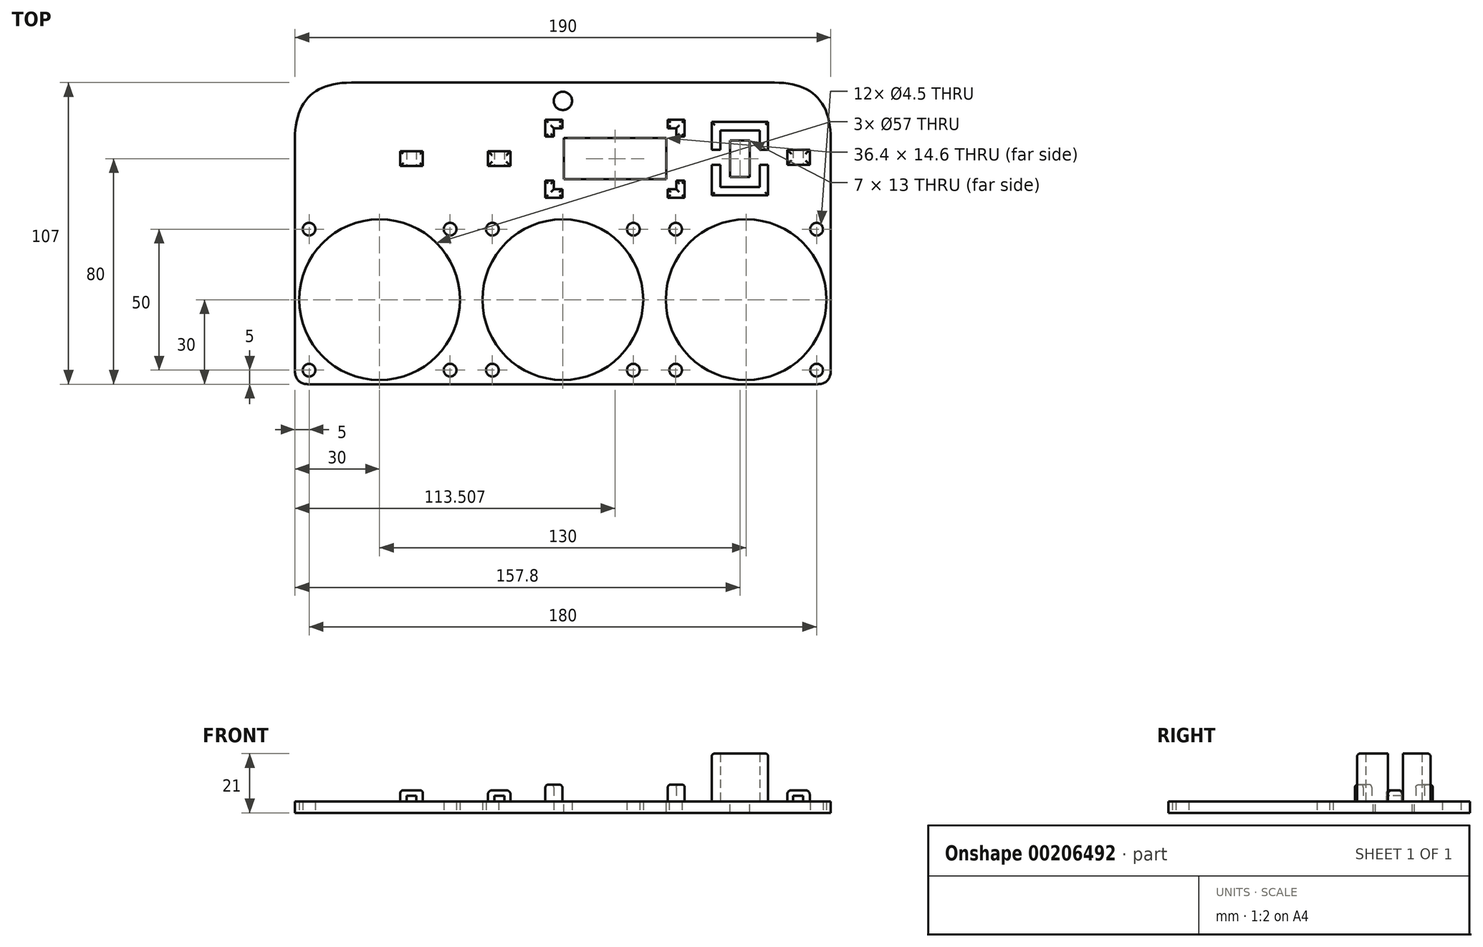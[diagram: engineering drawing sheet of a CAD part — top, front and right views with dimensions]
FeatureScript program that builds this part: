
annotation { "Feature Type Name" : "Feature", "Feature Type Description" : "" }
export const myFeature = defineFeature(function(context is Context, id is Id, definition is map)
    precondition{}
    {
        {
            var Q0;
            Q0=qCreatedBy(makeId("Top.planeOp"),FACE);
            var sketch = newSketch(context, id + "F0", { "sketchPlane" : qUnion([Q0])});
            skLineSegment(sketch, "E0", {"start": v(0, 124.98) * mm, "end": v(0, -119.8) * mm, "construction": true});
            skLineSegment(sketch, "E1.bottom", {"start": v(0, 0) * mm, "end": v(60, 0) * mm});
            skLineSegment(sketch, "E1.left", {"start": v(0, 0) * mm, "end": v(0, 60) * mm});
            skLineSegment(sketch, "E2.bottom", {"start": v(5, 5) * mm, "end": v(55, 5) * mm, "construction": true});
            skLineSegment(sketch, "E2.top", {"start": v(5, 55) * mm, "end": v(55, 55) * mm, "construction": true});
            skLineSegment(sketch, "E2.left", {"start": v(5, 5) * mm, "end": v(5, 55) * mm, "construction": true});
            skLineSegment(sketch, "E2.right", {"start": v(55, 5) * mm, "end": v(55, 55) * mm, "construction": true});
            skPoint(sketch, "E3.centerSnap0", {"position": v(55, 30) * mm});
            skPoint(sketch, "E3.centerSnap1", {"position": v(30, 55) * mm});
            skLineSegment(sketch, "E4.bottom", {"start": v(65, 0) * mm, "end": v(125, 0) * mm});
            skLineSegment(sketch, "E5.bottom", {"start": v(70, 5) * mm, "end": v(120, 5) * mm, "construction": true});
            skLineSegment(sketch, "E5.top", {"start": v(70, 55) * mm, "end": v(120, 55) * mm, "construction": true});
            skLineSegment(sketch, "E5.left", {"start": v(70, 5) * mm, "end": v(70, 55) * mm, "construction": true});
            skLineSegment(sketch, "E5.right", {"start": v(120, 5) * mm, "end": v(120, 55) * mm, "construction": true});
            skCircle(sketch, "E6", {"center": v(95, 30) * mm, "radius": 28.5 * mm});
            skPoint(sketch, "E6.centerSnap0", {"position": v(120, 30) * mm});
            skPoint(sketch, "E6.centerSnap1", {"position": v(95, 55) * mm});
            skLineSegment(sketch, "E7.bottom", {"start": v(130, 0) * mm, "end": v(190, 0) * mm});
            skLineSegment(sketch, "E7.right", {"start": v(190, 0) * mm, "end": v(190, 60) * mm});
            skLineSegment(sketch, "E8.bottom", {"start": v(135, 5) * mm, "end": v(185, 5) * mm, "construction": true});
            skLineSegment(sketch, "E8.top", {"start": v(135, 55) * mm, "end": v(185, 55) * mm, "construction": true});
            skLineSegment(sketch, "E8.left", {"start": v(135, 5) * mm, "end": v(135, 55) * mm, "construction": true});
            skLineSegment(sketch, "E8.right", {"start": v(185, 5) * mm, "end": v(185, 55) * mm, "construction": true});
            skCircle(sketch, "E9", {"center": v(160, 30) * mm, "radius": 28.5 * mm});
            skPoint(sketch, "E9.centerSnap0", {"position": v(185, 30) * mm});
            skPoint(sketch, "E9.centerSnap1", {"position": v(160, 55) * mm});
            skLineSegment(sketch, "E10", {"start": v(60, 0) * mm, "end": v(65, 0) * mm});
            skLineSegment(sketch, "E11", {"start": v(125, 0) * mm, "end": v(130, 0) * mm});
            skLineSegment(sketch, "E12.top", {"start": v(0, 107) * mm, "end": v(190, 107) * mm});
            skLineSegment(sketch, "E12.left", {"start": v(0, 60) * mm, "end": v(0, 107) * mm});
            skLineSegment(sketch, "E12.right", {"start": v(190, 60) * mm, "end": v(190, 107) * mm});
            skLineSegment(sketch, "E13", {"start": v(95, 107) * mm, "end": v(95, -15.16) * mm, "construction": true});
            skLineSegment(sketch, "E14", {"start": v(95, 100.5) * mm, "end": v(107.18, 100.5) * mm, "construction": true});
            skCircle(sketch, "E15", {"center": v(30, 30) * mm, "radius": 28.5 * mm});
            skSolve(sketch);
        }
        {
            var Q0;
            Q0=qSketchRegion(id+"F0",true);
            extrude(context, id + "F1", {"entities" : qUnion([Q0]), "depth" : 4 * mm});
        }
        {
            var Q0;
            Q0=sQuery(id+"F0.wireOp",VERTEX,"E14.start");
            var Q1;
            Q1=makeQuery(id+"F1.opExtrude","SWEPT_BODY",BODY,{"disambiguationData":[OSD([sQuery(id+"F0.wireOp",EDGE,"E1.bottom"),sQuery(id+"F0.wireOp",EDGE,"E1.left"),sQuery(id+"F0.wireOp",EDGE,"E3"),sQuery(id+"F0.wireOp",EDGE,"E4.bottom"),sQuery(id+"F0.wireOp",EDGE,"E6"),sQuery(id+"F0.wireOp",EDGE,"E7.bottom"),sQuery(id+"F0.wireOp",EDGE,"E7.right"),sQuery(id+"F0.wireOp",EDGE,"E9"),sQuery(id+"F0.wireOp",EDGE,"E10"),sQuery(id+"F0.wireOp",EDGE,"E11"),sQuery(id+"F0.wireOp",EDGE,"E12.top"),sQuery(id+"F0.wireOp",EDGE,"E12.left"),sQuery(id+"F0.wireOp",EDGE,"E12.right")])]});
            hole(context, id + "F2", {"style" : HoleStyle.SIMPLE, "endStyle" : HoleEndStyle.THROUGH, "oppositeDirection" : true, "holeDiameter" : 6.5 * mm, "locations" : qUnion([Q0]), "scope" : qUnion([Q1]), "isTappedThrough" : true});
        }
        {
            var Q0;
            Q0=sQuery(id+"F0.wireOp",VERTEX,"E2.top.start");
            var Q1;
            Q1=sQuery(id+"F0.wireOp",VERTEX,"E2.top.end");
            var Q2;
            Q2=sQuery(id+"F0.wireOp",VERTEX,"E2.bottom.start");
            var Q3;
            Q3=sQuery(id+"F0.wireOp",VERTEX,"E2.bottom.end");
            var Q4;
            Q4=sQuery(id+"F0.wireOp",VERTEX,"E5.left.end");
            var Q5;
            Q5=sQuery(id+"F0.wireOp",VERTEX,"E5.bottom.start");
            var Q6;
            Q6=sQuery(id+"F0.wireOp",VERTEX,"E5.bottom.end");
            var Q7;
            Q7=sQuery(id+"F0.wireOp",VERTEX,"E5.top.end");
            var Q8;
            Q8=sQuery(id+"F0.wireOp",VERTEX,"E8.left.end");
            var Q9;
            Q9=sQuery(id+"F0.wireOp",VERTEX,"E8.bottom.start");
            var Q10;
            Q10=sQuery(id+"F0.wireOp",VERTEX,"E8.bottom.end");
            var Q11;
            Q11=sQuery(id+"F0.wireOp",VERTEX,"E8.top.end");
            var Q12;
            Q12=makeQuery(id+"F1.opExtrude","SWEPT_BODY",BODY,{"disambiguationData":[OSD([sQuery(id+"F0.wireOp",EDGE,"E1.bottom"),sQuery(id+"F0.wireOp",EDGE,"E1.left"),sQuery(id+"F0.wireOp",EDGE,"E3"),sQuery(id+"F0.wireOp",EDGE,"E4.bottom"),sQuery(id+"F0.wireOp",EDGE,"E6"),sQuery(id+"F0.wireOp",EDGE,"E7.bottom"),sQuery(id+"F0.wireOp",EDGE,"E7.right"),sQuery(id+"F0.wireOp",EDGE,"E9"),sQuery(id+"F0.wireOp",EDGE,"E10"),sQuery(id+"F0.wireOp",EDGE,"E11"),sQuery(id+"F0.wireOp",EDGE,"E12.top"),sQuery(id+"F0.wireOp",EDGE,"E12.left"),sQuery(id+"F0.wireOp",EDGE,"E12.right")])]});
            hole(context, id + "F3", {"style" : HoleStyle.SIMPLE, "endStyle" : HoleEndStyle.THROUGH, "oppositeDirection" : true, "holeDiameter" : 4.5 * mm, "locations" : qUnion([Q0, Q1, Q2, Q3, Q4, Q5, Q6, Q7, Q8, Q9, Q10, Q11]), "scope" : qUnion([Q12]), "isTappedThrough" : true});
        }
        {
            var Q0;
            Q0=makeQuery(id+"F1.opExtrude","CAP_FACE",FACE,{"disambiguationData":[OSD([sQuery(id+"F0.wireOp",EDGE,"E1.bottom"),sQuery(id+"F0.wireOp",EDGE,"E1.left"),sQuery(id+"F0.wireOp",EDGE,"E3"),sQuery(id+"F0.wireOp",EDGE,"E4.bottom"),sQuery(id+"F0.wireOp",EDGE,"E6"),sQuery(id+"F0.wireOp",EDGE,"E7.bottom"),sQuery(id+"F0.wireOp",EDGE,"E7.right"),sQuery(id+"F0.wireOp",EDGE,"E9"),sQuery(id+"F0.wireOp",EDGE,"E10"),sQuery(id+"F0.wireOp",EDGE,"E11"),sQuery(id+"F0.wireOp",EDGE,"E12.top"),sQuery(id+"F0.wireOp",EDGE,"E12.left"),sQuery(id+"F0.wireOp",EDGE,"E12.right")])],"isStart":false});
            var sketch = newSketch(context, id + "F4", { "sketchPlane" : qUnion([Q0])});
            skLineSegment(sketch, "E16", {"start": v(160, 30) * mm, "end": v(160, 156.78) * mm, "construction": true});
            skLineSegment(sketch, "E17.bottom", {"start": v(150.8, 90) * mm, "end": v(164.8, 90) * mm});
            skLineSegment(sketch, "E17.top", {"start": v(150.8, 70) * mm, "end": v(164.8, 70) * mm});
            skLineSegment(sketch, "E17.left", {"start": v(150.8, 90) * mm, "end": v(150.8, 83.18) * mm});
            skLineSegment(sketch, "E17.right", {"start": v(164.8, 90) * mm, "end": v(164.8, 83.18) * mm});
            skLineSegment(sketch, "E18.0", {"start": v(147.8, 93) * mm, "end": v(147.8, 83.18) * mm});
            skLineSegment(sketch, "E18.1", {"start": v(147.8, 93) * mm, "end": v(167.8, 93) * mm});
            skLineSegment(sketch, "E18.2", {"start": v(167.8, 93) * mm, "end": v(167.8, 83.18) * mm});
            skLineSegment(sketch, "E18.3", {"start": v(147.8, 67) * mm, "end": v(167.8, 67) * mm});
            skLineSegment(sketch, "E19.0", {"start": v(185, 102) * mm, "end": v(5, 102) * mm});
            skLineSegment(sketch, "E19.1", {"start": v(185, 5) * mm, "end": v(185, 102) * mm});
            skLineSegment(sketch, "E19.2", {"start": v(5, 5) * mm, "end": v(185, 5) * mm});
            skLineSegment(sketch, "E19.3", {"start": v(5, 102) * mm, "end": v(5, 5) * mm});
            skLineSegment(sketch, "E20", {"start": v(164.8, 83.18) * mm, "end": v(167.8, 83.18) * mm});
            skLineSegment(sketch, "E21", {"start": v(164.8, 77.87) * mm, "end": v(167.8, 77.87) * mm});
            skLineSegment(sketch, "E22", {"start": v(150.8, 77.87) * mm, "end": v(147.8, 77.87) * mm});
            skLineSegment(sketch, "E23", {"start": v(150.8, 83.18) * mm, "end": v(147.8, 83.18) * mm});
            skLineSegment(sketch, "E24.trimOffspring", {"start": v(147.8, 77.87) * mm, "end": v(147.8, 67) * mm});
            skLineSegment(sketch, "E25.trimOffspring", {"start": v(150.8, 77.87) * mm, "end": v(150.8, 70) * mm});
            skLineSegment(sketch, "E26.trimOffspring", {"start": v(164.8, 77.87) * mm, "end": v(164.8, 70) * mm});
            skLineSegment(sketch, "E27.trimOffspring", {"start": v(167.8, 77.87) * mm, "end": v(167.8, 67) * mm});
            skLineSegment(sketch, "E28", {"start": v(91.8, 87.8) * mm, "end": v(91.8, 90.8) * mm});
            skLineSegment(sketch, "E29", {"start": v(91.8, 90.8) * mm, "end": v(94.8, 90.8) * mm});
            skLineSegment(sketch, "E30", {"start": v(94.8, 90.8) * mm, "end": v(94.8, 93.8) * mm});
            skLineSegment(sketch, "E31", {"start": v(94.8, 93.8) * mm, "end": v(88.8, 93.8) * mm});
            skLineSegment(sketch, "E32", {"start": v(88.8, 93.8) * mm, "end": v(88.8, 87.8) * mm});
            skLineSegment(sketch, "E33", {"start": v(88.8, 87.8) * mm, "end": v(91.8, 87.8) * mm});
            skLineSegment(sketch, "E34", {"start": v(82.5, 80) * mm, "end": v(142.35, 80) * mm, "construction": true});
            skLineSegment(sketch, "E35", {"start": v(113.5, 100.09) * mm, "end": v(113.5, 63.62) * mm, "construction": true});
            skLineSegment(sketch, "E36.MirrorCS", {"start": v(94.8, 66.2) * mm, "end": v(88.8, 66.2) * mm});
            skLineSegment(sketch, "E37.MirrorCS", {"start": v(94.8, 69.2) * mm, "end": v(94.8, 66.2) * mm});
            skLineSegment(sketch, "E38.MirrorCS", {"start": v(91.8, 69.2) * mm, "end": v(94.8, 69.2) * mm});
            skLineSegment(sketch, "E39.MirrorCS", {"start": v(88.8, 66.2) * mm, "end": v(88.8, 72.2) * mm});
            skLineSegment(sketch, "E40.MirrorCS", {"start": v(88.8, 72.2) * mm, "end": v(91.8, 72.2) * mm});
            skLineSegment(sketch, "E41.MirrorCS", {"start": v(91.8, 72.2) * mm, "end": v(91.8, 69.2) * mm});
            skLineSegment(sketch, "E42.MirrorCS", {"start": v(138.2, 72.2) * mm, "end": v(135.2, 72.2) * mm});
            skLineSegment(sketch, "E43.MirrorCS", {"start": v(132.2, 66.2) * mm, "end": v(138.2, 66.2) * mm});
            skLineSegment(sketch, "E44.MirrorCS", {"start": v(138.2, 66.2) * mm, "end": v(138.2, 72.2) * mm});
            skLineSegment(sketch, "E45.MirrorCS", {"start": v(135.2, 69.2) * mm, "end": v(132.2, 69.2) * mm});
            skLineSegment(sketch, "E46.MirrorCS", {"start": v(135.2, 72.2) * mm, "end": v(135.2, 69.2) * mm});
            skLineSegment(sketch, "E47.MirrorCS", {"start": v(132.2, 69.2) * mm, "end": v(132.2, 66.2) * mm});
            skLineSegment(sketch, "E48.MirrorCS", {"start": v(132.2, 90.8) * mm, "end": v(132.2, 93.8) * mm});
            skLineSegment(sketch, "E49.MirrorCS", {"start": v(138.2, 87.8) * mm, "end": v(135.2, 87.8) * mm});
            skLineSegment(sketch, "E50.MirrorCS", {"start": v(135.2, 87.8) * mm, "end": v(135.2, 90.8) * mm});
            skLineSegment(sketch, "E51.MirrorCS", {"start": v(138.2, 93.8) * mm, "end": v(138.2, 87.8) * mm});
            skLineSegment(sketch, "E52.MirrorCS", {"start": v(135.2, 90.8) * mm, "end": v(132.2, 90.8) * mm});
            skLineSegment(sketch, "E53.MirrorCS", {"start": v(132.2, 93.8) * mm, "end": v(138.2, 93.8) * mm});
            skPoint(sketch, "E54.firstSnap0", {"position": v(135.2, 93.8) * mm});
            skLineSegment(sketch, "E55.bottom", {"start": v(91.8, 90.8) * mm, "end": v(135.2, 90.8) * mm, "construction": true});
            skLineSegment(sketch, "E55.top", {"start": v(91.8, 69.2) * mm, "end": v(135.2, 69.2) * mm, "construction": true});
            skLineSegment(sketch, "E55.left", {"start": v(91.8, 90.8) * mm, "end": v(91.8, 69.2) * mm, "construction": true});
            skLineSegment(sketch, "E55.right", {"start": v(135.2, 90.8) * mm, "end": v(135.2, 69.2) * mm, "construction": true});
            skLineSegment(sketch, "E56.0", {"start": v(95.3, 87.3) * mm, "end": v(131.7, 87.3) * mm});
            skLineSegment(sketch, "E56.1", {"start": v(95.3, 87.3) * mm, "end": v(95.3, 72.7) * mm});
            skLineSegment(sketch, "E56.2", {"start": v(95.3, 72.7) * mm, "end": v(131.7, 72.7) * mm});
            skLineSegment(sketch, "E56.3", {"start": v(131.7, 87.3) * mm, "end": v(131.7, 72.7) * mm});
            skLineSegment(sketch, "E57.left", {"start": v(150.8, 90) * mm, "end": v(150.8, 70) * mm});
            skLineSegment(sketch, "E57.right", {"start": v(164.8, 90) * mm, "end": v(164.8, 70) * mm});
            skLineSegment(sketch, "E58.0", {"start": v(154.3, 86.5) * mm, "end": v(154.3, 73.5) * mm});
            skLineSegment(sketch, "E58.1", {"start": v(154.3, 86.5) * mm, "end": v(161.3, 86.5) * mm});
            skLineSegment(sketch, "E58.2", {"start": v(161.3, 86.5) * mm, "end": v(161.3, 73.5) * mm});
            skLineSegment(sketch, "E58.3", {"start": v(154.3, 73.5) * mm, "end": v(161.3, 73.5) * mm});
            skPoint(sketch, "E59", {"position": v(150.8, 80) * mm});
            skLineSegment(sketch, "E60.bottom", {"start": v(174.55, 83.18) * mm, "end": v(182.55, 83.18) * mm});
            skLineSegment(sketch, "E60.top", {"start": v(174.55, 77.87) * mm, "end": v(182.55, 77.87) * mm});
            skLineSegment(sketch, "E60.left", {"start": v(174.55, 83.18) * mm, "end": v(174.55, 77.87) * mm});
            skLineSegment(sketch, "E60.right", {"start": v(182.55, 83.18) * mm, "end": v(182.55, 77.87) * mm});
            skLineSegment(sketch, "E61.bottom", {"start": v(68.44, 82.7) * mm, "end": v(76.44, 82.7) * mm});
            skLineSegment(sketch, "E61.top", {"start": v(68.44, 77.4) * mm, "end": v(76.44, 77.4) * mm});
            skLineSegment(sketch, "E61.left", {"start": v(68.44, 82.7) * mm, "end": v(68.44, 77.4) * mm});
            skLineSegment(sketch, "E61.right", {"start": v(76.44, 82.7) * mm, "end": v(76.44, 77.4) * mm});
            skLineSegment(sketch, "E62.bottom", {"start": v(45.36, 77.4) * mm, "end": v(37.36, 77.4) * mm});
            skLineSegment(sketch, "E62.top", {"start": v(45.36, 82.7) * mm, "end": v(37.36, 82.7) * mm});
            skLineSegment(sketch, "E62.left", {"start": v(45.36, 77.4) * mm, "end": v(45.36, 82.7) * mm});
            skLineSegment(sketch, "E62.right", {"start": v(37.36, 77.4) * mm, "end": v(37.36, 82.7) * mm});
            skSolve(sketch);
        }
        {
            var Q0;
            Q0=makeQuery(id+"F4.imprint","IMPRINT",FACE,{"disambiguationData":[TD([[makeQuery(id+"F4.imprint","IMPRINT",EDGE,{"derivedFrom":sQuery(id+"F4.wireOp",EDGE,"E18.0")}),1.0]])]});
            var Q1;
            Q1=makeQuery(id+"F4.imprint","IMPRINT",FACE,{"disambiguationData":[TD([[makeQuery(id+"F4.imprint","IMPRINT",EDGE,{"derivedFrom":sQuery(id+"F4.wireOp",EDGE,"E18.3")}),1.0]])]});
            extrude(context, id + "F5", {"entities" : qUnion([Q0, Q1]), "operationType" : NewBodyOperationType.ADD, "depth" : 17 * mm});
        }
        {
            var Q0;
            Q0=makeQuery(id+"F4.imprint","IMPRINT",FACE,{"disambiguationData":[TD([[makeQuery(id+"F4.imprint","IMPRINT",EDGE,{"derivedFrom":sQuery(id+"F4.wireOp",EDGE,"E48.MirrorCS")}),-1.0]])]});
            var Q1;
            Q1=makeQuery(id+"F4.imprint","IMPRINT",FACE,{"disambiguationData":[TD([[makeQuery(id+"F4.imprint","IMPRINT",EDGE,{"derivedFrom":sQuery(id+"F4.wireOp",EDGE,"E42.MirrorCS")}),1.0]])]});
            var Q2;
            Q2=makeQuery(id+"F4.imprint","IMPRINT",FACE,{"disambiguationData":[TD([[makeQuery(id+"F4.imprint","IMPRINT",EDGE,{"derivedFrom":sQuery(id+"F4.wireOp",EDGE,"E36.MirrorCS")}),-1.0]])]});
            var Q3;
            Q3=makeQuery(id+"F4.imprint","IMPRINT",FACE,{"disambiguationData":[TD([[makeQuery(id+"F4.imprint","IMPRINT",EDGE,{"derivedFrom":sQuery(id+"F4.wireOp",EDGE,"E28")}),1.0]])]});
            extrude(context, id + "F6", {"entities" : qUnion([Q0, Q1, Q2, Q3]), "operationType" : NewBodyOperationType.ADD, "depth" : 6 * mm});
        }
        {
            var Q0;
            Q0=makeQuery(id+"F4.imprint","IMPRINT",FACE,{"disambiguationData":[TD([[makeQuery(id+"F4.imprint","IMPRINT",EDGE,{"derivedFrom":sQuery(id+"F4.wireOp",EDGE,"E56.0")}),-1.0]])]});
            extrude(context, id + "F7", {"entities" : qUnion([Q0]), "operationType" : NewBodyOperationType.REMOVE, "oppositeDirection" : true, "depth" : 25 * mm});
        }
        {
            var Q0;
            Q0=makeQuery(id+"F4.imprint","IMPRINT",FACE,{"disambiguationData":[TD([[makeQuery(id+"F4.imprint","IMPRINT",EDGE,{"derivedFrom":sQuery(id+"F4.wireOp",EDGE,"E58.0")}),1.0]])]});
            extrude(context, id + "F8", {"entities" : qUnion([Q0]), "operationType" : NewBodyOperationType.REMOVE, "oppositeDirection" : true, "depth" : 25 * mm});
        }
        {
            var Q0;
            Q0=makeQuery(id+"F1.opExtrude","SWEPT_EDGE",EDGE,{"disambiguationData":[OSD([sQuery(id+"F0.wireOp",EDGE,"E12.top"),sQuery(id+"F0.wireOp",EDGE,"E12.left")])]});
            var Q1;
            Q1=makeQuery(id+"F1.opExtrude","SWEPT_EDGE",EDGE,{"disambiguationData":[OSD([sQuery(id+"F0.wireOp",EDGE,"E12.top"),sQuery(id+"F0.wireOp",EDGE,"E12.right")])]});
            fillet(context, id + "F9", {"entities" : qUnion([Q0, Q1]), "radius" : 20 * mm, "tangentPropagation" : true, "rho" : 0.5, "crossSection" : FilletCrossSection.CONIC, "allowEdgeOverflow" : false});
        }
        {
            var Q0;
            Q0=makeQuery(id+"F1.opExtrude","SWEPT_EDGE",EDGE,{"disambiguationData":[OSD([sQuery(id+"F0.wireOp",EDGE,"E1.bottom"),sQuery(id+"F0.wireOp",EDGE,"E1.left")])]});
            var Q1;
            Q1=makeQuery(id+"F1.opExtrude","SWEPT_EDGE",EDGE,{"disambiguationData":[OSD([sQuery(id+"F0.wireOp",EDGE,"E7.bottom"),sQuery(id+"F0.wireOp",EDGE,"E7.right")])]});
            fillet(context, id + "F10", {"entities" : qUnion([Q0, Q1]), "radius" : 5 * mm, "tangentPropagation" : true, "rho" : 0.5, "crossSection" : FilletCrossSection.CONIC, "allowEdgeOverflow" : false});
        }
        {
            var Q0;
            Q0=makeQuery(id+"F4.imprint","IMPRINT",FACE,{"disambiguationData":[TD([[makeQuery(id+"F4.imprint","IMPRINT",EDGE,{"derivedFrom":sQuery(id+"F4.wireOp",EDGE,"E60.bottom")}),-1.0]])]});
            var Q1;
            Q1=makeQuery(id+"F4.imprint","IMPRINT",FACE,{"disambiguationData":[TD([[makeQuery(id+"F4.imprint","IMPRINT",EDGE,{"derivedFrom":sQuery(id+"F4.wireOp",EDGE,"E61.bottom")}),-1.0]])]});
            var Q2;
            Q2=makeQuery(id+"F4.imprint","IMPRINT",FACE,{"disambiguationData":[TD([[makeQuery(id+"F4.imprint","IMPRINT",EDGE,{"derivedFrom":sQuery(id+"F4.wireOp",EDGE,"E62.bottom")}),-1.0]])]});
            extrude(context, id + "F11", {"entities" : qUnion([Q0, Q1, Q2]), "operationType" : NewBodyOperationType.ADD, "depth" : 4 * mm});
        }
        {
            var Q0;
            Q0=makeQuery(id+"F11.opExtrude","SWEPT_FACE",FACE,{"disambiguationData":[OSD([sQuery(id+"F4.wireOp",EDGE,"E60.top")])]});
            var sketch = newSketch(context, id + "F12", { "sketchPlane" : qUnion([Q0])});
            skPoint(sketch, "E63.oppositeSnap0", {"position": v(174.55, 6) * mm});
            skLineSegment(sketch, "E63.bottom", {"start": v(176.7, 4) * mm, "end": v(180.23, 4) * mm});
            skLineSegment(sketch, "E63.top", {"start": v(176.7, 6) * mm, "end": v(180.23, 6) * mm});
            skLineSegment(sketch, "E63.left", {"start": v(176.7, 4) * mm, "end": v(176.7, 6) * mm});
            skLineSegment(sketch, "E63.right", {"start": v(180.23, 4) * mm, "end": v(180.23, 6) * mm});
            skSolve(sketch);
        }
        {
            var Q0;
            Q0=qSketchRegion(id+"F12",true);
            extrude(context, id + "F13", {"entities" : qUnion([Q0]), "operationType" : NewBodyOperationType.REMOVE, "oppositeDirection" : true, "depth" : 25 * mm});
        }
        {
            var Q0;
            Q0=makeQuery(id+"F11.opExtrude","CAP_EDGE",EDGE,{"disambiguationData":[OSD([sQuery(id+"F4.wireOp",EDGE,"E60.left")])],"isStart":false});
            var Q1;
            Q1=makeQuery(id+"F11.opExtrude","CAP_EDGE",EDGE,{"disambiguationData":[OSD([sQuery(id+"F4.wireOp",EDGE,"E60.right")])],"isStart":false});
            var Q2;
            Q2=makeQuery(id+"F11.opExtrude","CAP_EDGE",EDGE,{"disambiguationData":[OSD([sQuery(id+"F4.wireOp",EDGE,"E60.bottom")])],"isStart":false});
            var Q3;
            Q3=makeQuery(id+"F11.opExtrude","CAP_EDGE",EDGE,{"disambiguationData":[OSD([sQuery(id+"F4.wireOp",EDGE,"E60.top")])],"isStart":false});
            fillet(context, id + "F14", {"entities" : qUnion([Q0, Q1, Q2, Q3]), "radius" : 1.5 * mm, "tangentPropagation" : true, "allowEdgeOverflow" : false});
        }
        {
            var Q0;
            Q0=makeQuery(id+"F5.opExtrude","CAP_EDGE",EDGE,{"disambiguationData":[OSD([sQuery(id+"F4.wireOp",EDGE,"E24.trimOffspring")])],"isStart":false});
            var Q1;
            Q1=makeQuery(id+"F5.opExtrude","CAP_EDGE",EDGE,{"disambiguationData":[OSD([sQuery(id+"F4.wireOp",EDGE,"E18.3")])],"isStart":false});
            var Q2;
            Q2=makeQuery(id+"F5.opExtrude","CAP_EDGE",EDGE,{"disambiguationData":[OSD([sQuery(id+"F4.wireOp",EDGE,"E27.trimOffspring")])],"isStart":false});
            var Q3;
            Q3=makeQuery(id+"F5.opExtrude","CAP_EDGE",EDGE,{"disambiguationData":[OSD([sQuery(id+"F4.wireOp",EDGE,"E18.0")])],"isStart":false});
            var Q4;
            Q4=makeQuery(id+"F5.opExtrude","CAP_EDGE",EDGE,{"disambiguationData":[OSD([sQuery(id+"F4.wireOp",EDGE,"E18.1")])],"isStart":false});
            var Q5;
            Q5=makeQuery(id+"F5.opExtrude","CAP_EDGE",EDGE,{"disambiguationData":[OSD([sQuery(id+"F4.wireOp",EDGE,"E18.2")])],"isStart":false});
            fillet(context, id + "F15", {"entities" : qUnion([Q0, Q1, Q2, Q3, Q4, Q5]), "radius" : 1 * mm, "tangentPropagation" : true, "allowEdgeOverflow" : false});
        }
        {
            var Q0;
            Q0=makeQuery(id+"F11.opExtrude","SWEPT_FACE",FACE,{"disambiguationData":[OSD([sQuery(id+"F4.wireOp",EDGE,"E61.top")])]});
            var sketch = newSketch(context, id + "F16", { "sketchPlane" : qUnion([Q0])});
            skLineSegment(sketch, "E64.bottom", {"start": v(70.73, 4) * mm, "end": v(74.23, 4) * mm});
            skLineSegment(sketch, "E64.top", {"start": v(70.73, 6) * mm, "end": v(74.23, 6) * mm});
            skLineSegment(sketch, "E64.left", {"start": v(70.73, 4) * mm, "end": v(70.73, 6) * mm});
            skLineSegment(sketch, "E64.right", {"start": v(74.23, 4) * mm, "end": v(74.23, 6) * mm});
            skSolve(sketch);
        }
        {
            var Q0;
            Q0=makeQuery(id+"F16.imprint","IMPRINT",FACE,{"disambiguationData":[TD([[makeQuery(id+"F16.imprint","IMPRINT",EDGE,{"derivedFrom":sQuery(id+"F16.wireOp",EDGE,"E64.bottom")}),1.0]])]});
            extrude(context, id + "F17", {"entities" : qUnion([Q0]), "operationType" : NewBodyOperationType.REMOVE, "oppositeDirection" : true, "depth" : 25 * mm});
        }
        {
            var Q0;
            Q0=makeQuery(id+"F11.opExtrude","CAP_FACE",FACE,{"disambiguationData":[OSD([sQuery(id+"F4.wireOp",EDGE,"E61.bottom"),sQuery(id+"F4.wireOp",EDGE,"E61.top"),sQuery(id+"F4.wireOp",EDGE,"E61.left"),sQuery(id+"F4.wireOp",EDGE,"E61.right")])],"isStart":false});
            fillet(context, id + "F18", {"entities" : qUnion([Q0]), "radius" : 1.5 * mm, "tangentPropagation" : true, "allowEdgeOverflow" : false});
        }
        {
            var Q0;
            Q0=makeQuery(id+"F11.opExtrude","SWEPT_FACE",FACE,{"disambiguationData":[OSD([sQuery(id+"F4.wireOp",EDGE,"E62.bottom")])]});
            var sketch = newSketch(context, id + "F19", { "sketchPlane" : qUnion([Q0])});
            skLineSegment(sketch, "E65.bottom", {"start": v(39.57, 4) * mm, "end": v(43.07, 4) * mm});
            skLineSegment(sketch, "E65.top", {"start": v(39.57, 6) * mm, "end": v(43.07, 6) * mm});
            skLineSegment(sketch, "E65.left", {"start": v(39.57, 4) * mm, "end": v(39.57, 6) * mm});
            skLineSegment(sketch, "E65.right", {"start": v(43.07, 4) * mm, "end": v(43.07, 6) * mm});
            skSolve(sketch);
        }
        {
            var Q0;
            Q0=makeQuery(id+"F19.imprint","IMPRINT",FACE,{"disambiguationData":[TD([[makeQuery(id+"F19.imprint","IMPRINT",EDGE,{"derivedFrom":sQuery(id+"F19.wireOp",EDGE,"E65.bottom")}),-1.0]])]});
            extrude(context, id + "F20", {"entities" : qUnion([Q0]), "operationType" : NewBodyOperationType.REMOVE, "oppositeDirection" : true, "depth" : 25 * mm});
        }
        {
            var Q0;
            Q0=makeQuery(id+"F11.opExtrude","CAP_FACE",FACE,{"disambiguationData":[OSD([sQuery(id+"F4.wireOp",EDGE,"E62.bottom"),sQuery(id+"F4.wireOp",EDGE,"E62.top"),sQuery(id+"F4.wireOp",EDGE,"E62.left"),sQuery(id+"F4.wireOp",EDGE,"E62.right")])],"isStart":false});
            fillet(context, id + "F21", {"entities" : qUnion([Q0]), "radius" : 1 * mm, "tangentPropagation" : true, "allowEdgeOverflow" : false});
        }
        {
            var Q0;
            Q0=makeQuery(id+"F6.opExtrude","CAP_FACE",FACE,{"disambiguationData":[OSD([sQuery(id+"F4.wireOp",EDGE,"E28"),sQuery(id+"F4.wireOp",EDGE,"E29"),sQuery(id+"F4.wireOp",EDGE,"E30"),sQuery(id+"F4.wireOp",EDGE,"E31"),sQuery(id+"F4.wireOp",EDGE,"E32"),sQuery(id+"F4.wireOp",EDGE,"E33")])],"isStart":false});
            var Q1;
            Q1=makeQuery(id+"F6.opExtrude","CAP_FACE",FACE,{"disambiguationData":[OSD([sQuery(id+"F4.wireOp",EDGE,"E48.MirrorCS"),sQuery(id+"F4.wireOp",EDGE,"E49.MirrorCS"),sQuery(id+"F4.wireOp",EDGE,"E50.MirrorCS"),sQuery(id+"F4.wireOp",EDGE,"E51.MirrorCS"),sQuery(id+"F4.wireOp",EDGE,"E52.MirrorCS"),sQuery(id+"F4.wireOp",EDGE,"E53.MirrorCS")])],"isStart":false});
            var Q2;
            Q2=makeQuery(id+"F6.opExtrude","CAP_FACE",FACE,{"disambiguationData":[OSD([sQuery(id+"F4.wireOp",EDGE,"E42.MirrorCS"),sQuery(id+"F4.wireOp",EDGE,"E43.MirrorCS"),sQuery(id+"F4.wireOp",EDGE,"E44.MirrorCS"),sQuery(id+"F4.wireOp",EDGE,"E45.MirrorCS"),sQuery(id+"F4.wireOp",EDGE,"E46.MirrorCS"),sQuery(id+"F4.wireOp",EDGE,"E47.MirrorCS")])],"isStart":false});
            var Q3;
            Q3=makeQuery(id+"F6.opExtrude","CAP_FACE",FACE,{"disambiguationData":[OSD([sQuery(id+"F4.wireOp",EDGE,"E36.MirrorCS"),sQuery(id+"F4.wireOp",EDGE,"E37.MirrorCS"),sQuery(id+"F4.wireOp",EDGE,"E38.MirrorCS"),sQuery(id+"F4.wireOp",EDGE,"E39.MirrorCS"),sQuery(id+"F4.wireOp",EDGE,"E40.MirrorCS"),sQuery(id+"F4.wireOp",EDGE,"E41.MirrorCS")])],"isStart":false});
            fillet(context, id + "F22", {"entities" : qUnion([Q0, Q1, Q2, Q3]), "radius" : 1 * mm, "tangentPropagation" : true, "allowEdgeOverflow" : false});
        }
    });
